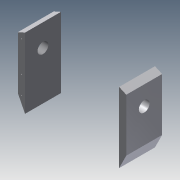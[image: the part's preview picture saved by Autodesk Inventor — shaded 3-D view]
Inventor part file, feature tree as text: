
AUTODESK INVENTOR PART (.ipt)
format: ipt  version: 2013 (Build 170138000, 138)  size: 112,128 bytes
history: native  units: mm
features: sketch x4, hole x2, extrude x1
ambient origin geometry x8: Origin, YZ Plane, XZ Plane, XY Plane, X Axis, Y Axis, Z Axis, Center Point
bodies: Solid1 (feature_tree)
feature tree (7):
  extrude  "Extrusion1"  Depth=73.5mm
  hole  "Hole1"  [1 undecoded]
  hole  "Hole2"  [1 undecoded]
  sketch  "Sketch5"  dims[d16=15.0mm d17=15.0mm d18=6.0mm d19=4.0mm d20=2.0mm d21=90.0deg d22=151.0mm d23=0.0mm d24=5.0mm d25=5.0mm d26=48.0mm d27=5.0mm d28=5.0mm d29=2.0mm d30=6.0mm d31=4.0mm d32=2.0mm d33=90.0deg d34=50.0mm d35=0.0mm]
  sketch  "Sketch1"  dims[d3=10.0mm d4=73.5mm]
  sketch  "Sketch2"  dims[d5=10.0mm d8=10.0mm]
  sketch  "Sketch3"  dims[d9=73.5mm d12=50.0mm d13=0.0mm]
note: 2 required parameter values undecoded (feature->parameter linkage not recoverable at this tier; creation-order binding heuristic only, values carry confidence <= 0.55)
